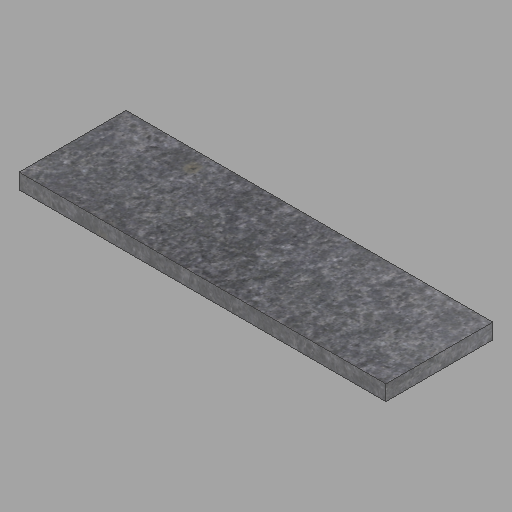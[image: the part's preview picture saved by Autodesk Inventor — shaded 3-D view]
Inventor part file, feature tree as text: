
AUTODESK INVENTOR PART (.ipt)
format: ipt  version: 2023 (Build 270158000, 158)  size: 202,752 bytes
history: native  units: in
note: dims shown in document units (in); Inventor stores cm internally (conversion verified against a paired STEP export)
features: other x1, extrude x1, sketch x1
ambient origin geometry x8: Origin, YZ Plane, XZ Plane, XY Plane, X Axis, Y Axis, Z Axis, Center Point
bodies: Solid1 (feature_tree)
feature tree (3):
  other  "2x14x48-2"
  extrude  "Extrusion1"  Depth=14.0in
  sketch  "Sketch1"  dims[d0=2.0in d1=14.0in d2=48.0in d3=0.0in]
